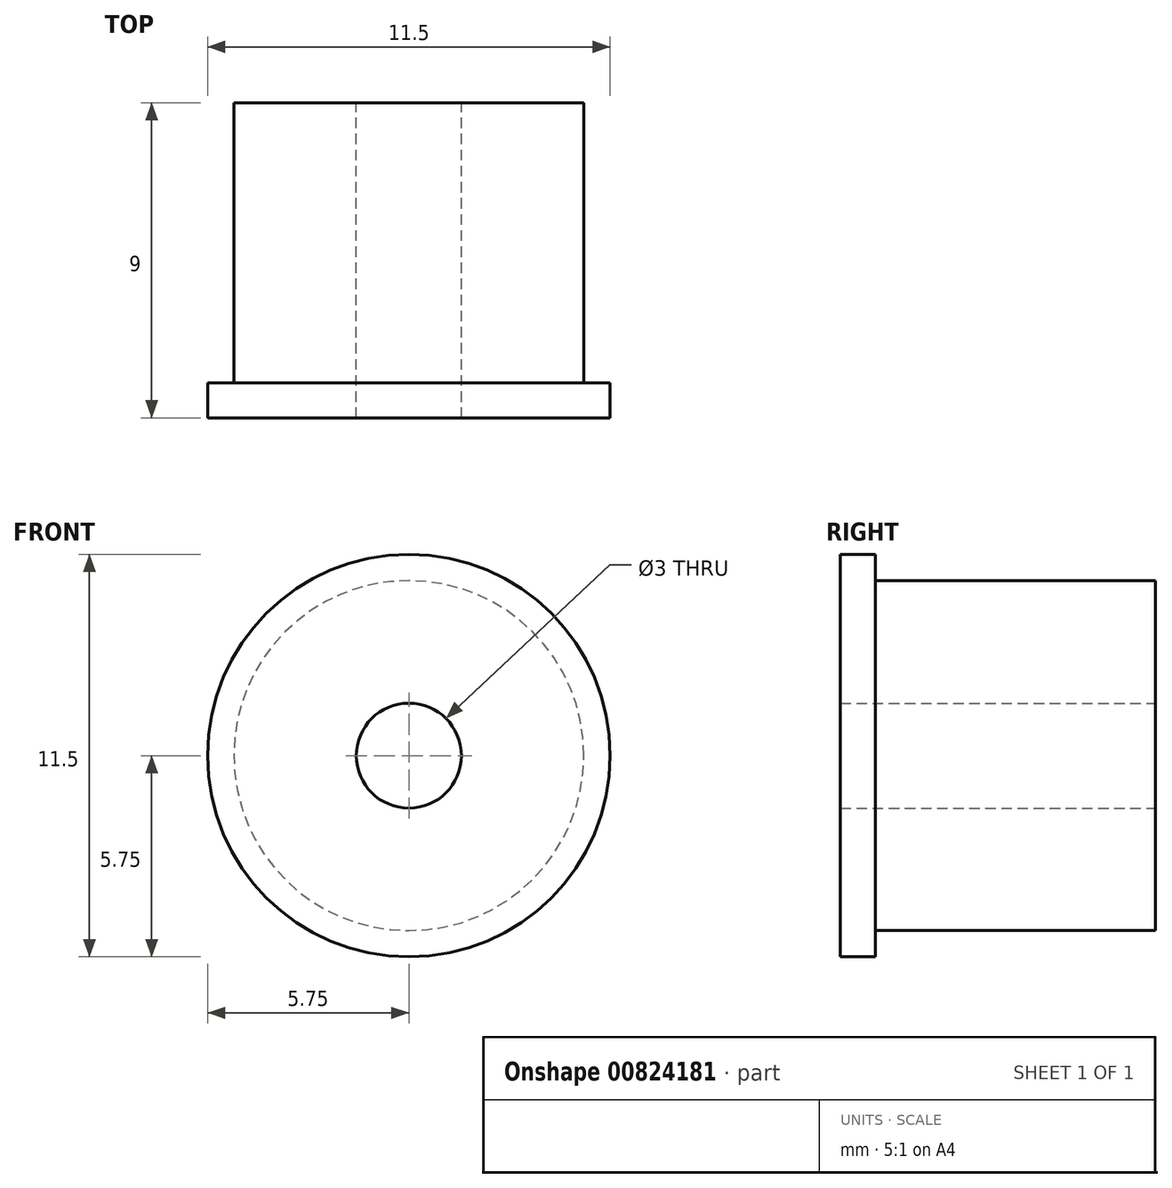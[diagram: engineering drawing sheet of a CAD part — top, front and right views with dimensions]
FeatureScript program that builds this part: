
annotation { "Feature Type Name" : "Feature", "Feature Type Description" : "" }
export const myFeature = defineFeature(function(context is Context, id is Id, definition is map)
    precondition{}
    {
        {
            var Q0;
            Q0=qCreatedBy(makeId("Front.planeOp"),FACE);
            var sketch = newSketch(context, id + "F0", { "sketchPlane" : qUnion([Q0])});
            skCircle(sketch, "E0", {"center": v(0, 0) * mm, "radius": 5 * mm});
            skSolve(sketch);
        }
        {
            var Q0;
            Q0 = qSketchRegion(id + "F0", true);
            extrude(context, id + "F1", {"entities" : qUnion([Q0]), "depth" : 8 * mm, "offsetDistance" : 25 * mm});
        }
        {
            var Q0;
            Q0=makeQuery(id+"F1.opExtrude","CAP_FACE",FACE,{"disambiguationData":[OSD([sQuery(id+"F0.wireOp",EDGE,"E0")])],"isStart":false});
            var sketch = newSketch(context, id + "F2", { "sketchPlane" : qUnion([Q0])});
            skCircle(sketch, "E1", {"center": v(0, 0) * mm, "radius": 5.75 * mm});
            skSolve(sketch);
        }
        {
            var Q0;
            Q0 = qSketchRegion(id + "F2", true);
            extrude(context, id + "F3", {"entities" : qUnion([Q0]), "operationType" : NewBodyOperationType.ADD, "depth" : 1 * mm, "offsetDistance" : 25 * mm});
        }
        {
            var Q0;
            Q0=makeQuery(id+"F1.opExtrude","CAP_FACE",FACE,{"disambiguationData":[OSD([sQuery(id+"F0.wireOp",EDGE,"E0")])],"isStart":true});
            var sketch = newSketch(context, id + "F4", { "sketchPlane" : qUnion([Q0])});
            skCircle(sketch, "E2", {"center": v(0, 0) * mm, "radius": 1.5 * mm});
            skSolve(sketch);
        }
        {
            var Q0;
            Q0 = qSketchRegion(id + "F4", true);
            extrude(context, id + "F5", {"entities" : qUnion([Q0]), "operationType" : NewBodyOperationType.REMOVE, "oppositeDirection" : true, "depth" : 25 * mm, "offsetDistance" : 25 * mm});
        }
    });
